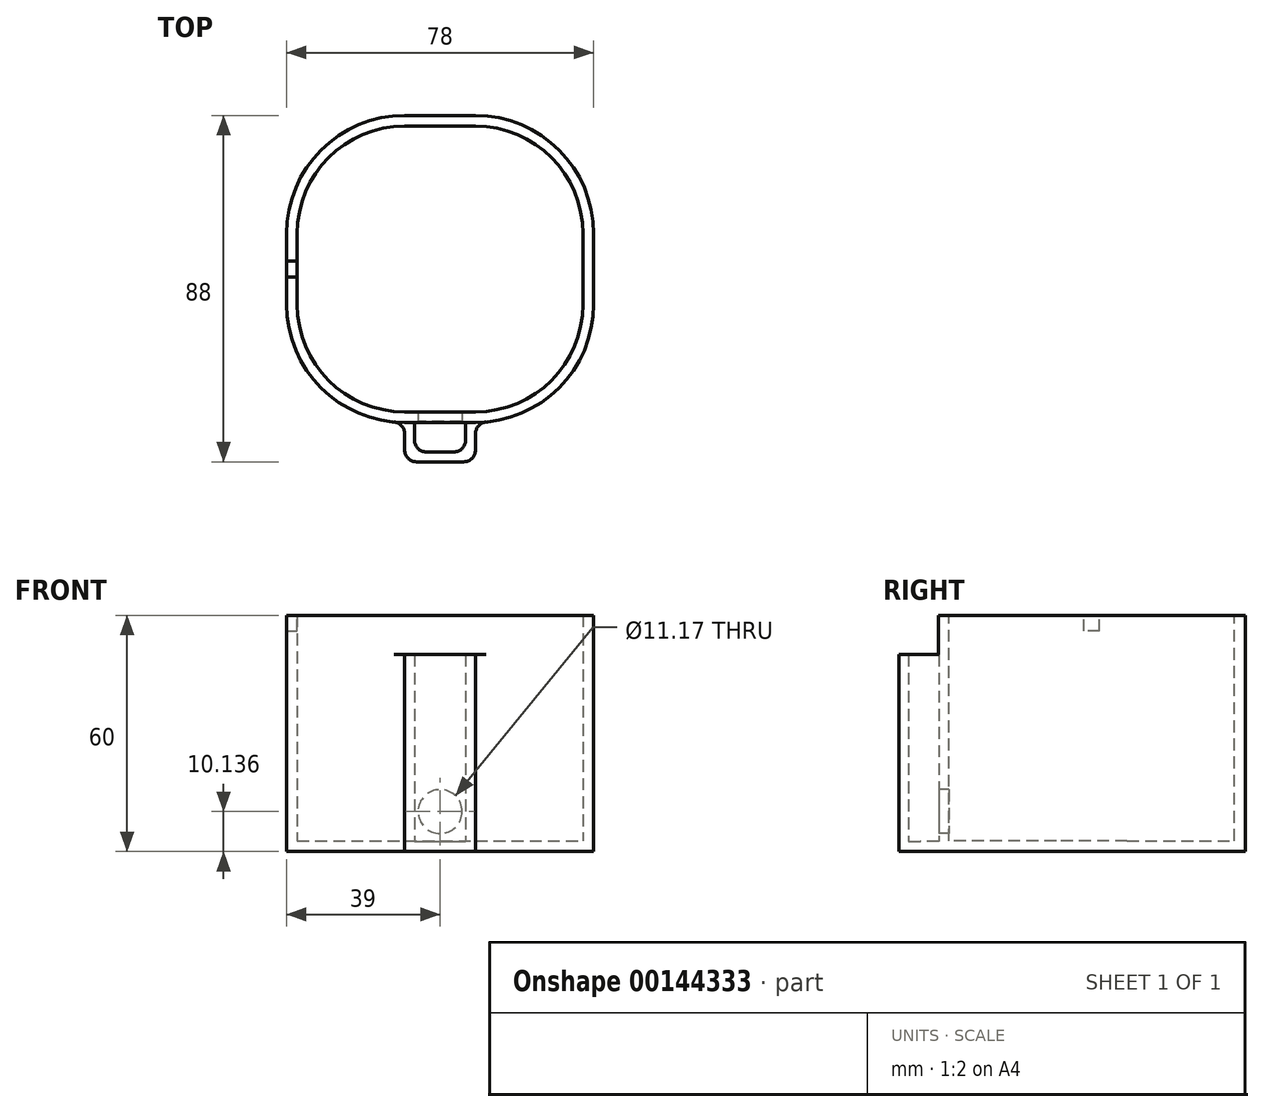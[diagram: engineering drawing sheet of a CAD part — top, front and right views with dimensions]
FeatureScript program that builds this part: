
annotation { "Feature Type Name" : "Feature", "Feature Type Description" : "" }
export const myFeature = defineFeature(function(context is Context, id is Id, definition is map)
    precondition{}
    {
        {
            var Q0;
            Q0=qCreatedBy(makeId("Top.planeOp"),FACE);
            var sketch = newSketch(context, id + "F0", { "sketchPlane" : qUnion([Q0])});
            skLineSegment(sketch, "E0.bottom", {"start": v(-39, 39) * mm, "end": v(39, 39) * mm});
            skLineSegment(sketch, "E0.top", {"start": v(-39, -39) * mm, "end": v(39, -39) * mm});
            skLineSegment(sketch, "E0.left", {"start": v(-39, 39) * mm, "end": v(-39, -39) * mm});
            skLineSegment(sketch, "E0.right", {"start": v(39, 39) * mm, "end": v(39, -39) * mm});
            skSolve(sketch);
        }
        {
            var Q0;
            Q0=makeQuery(id+"F0.imprint","IMPRINT",FACE,{"disambiguationData":[TD([[makeQuery(id+"F0.imprint","IMPRINT",EDGE,{"derivedFrom":sQuery(id+"F0.wireOp",EDGE,"E0.bottom")}),-1.0]])]});
            extrude(context, id + "F1", {"entities" : qUnion([Q0]), "depth" : 60 * mm});
        }
        {
            var Q0;
            Q0=makeQuery(id+"F1.opExtrude","SWEPT_EDGE",EDGE,{"disambiguationData":[OSD([sQuery(id+"F0.wireOp",EDGE,"E0.top"),sQuery(id+"F0.wireOp",EDGE,"E0.left")])]});
            var Q1;
            Q1=makeQuery(id+"F1.opExtrude","SWEPT_EDGE",EDGE,{"disambiguationData":[OSD([sQuery(id+"F0.wireOp",EDGE,"E0.top"),sQuery(id+"F0.wireOp",EDGE,"E0.right")])]});
            var Q2;
            Q2=makeQuery(id+"F1.opExtrude","SWEPT_EDGE",EDGE,{"disambiguationData":[OSD([sQuery(id+"F0.wireOp",EDGE,"E0.bottom"),sQuery(id+"F0.wireOp",EDGE,"E0.right")])]});
            var Q3;
            Q3=makeQuery(id+"F1.opExtrude","SWEPT_EDGE",EDGE,{"disambiguationData":[OSD([sQuery(id+"F0.wireOp",EDGE,"E0.bottom"),sQuery(id+"F0.wireOp",EDGE,"E0.left")])]});
            fillet(context, id + "F2", {"entities" : qUnion([Q0, Q1, Q2, Q3]), "radius" : 30 * mm, "tangentPropagation" : true, "allowEdgeOverflow" : false});
        }
        {
            var Q0;
            Q0=qCreatedBy(makeId("Top.planeOp"),FACE);
            var sketch = newSketch(context, id + "F3", { "sketchPlane" : qUnion([Q0])});
            skPoint(sketch, "E1", {"position": v(-9, -39) * mm});
            skPoint(sketch, "E2", {"position": v(9, -39) * mm});
            skLineSegment(sketch, "E3.bottom", {"start": v(-9, -39) * mm, "end": v(9, -39) * mm});
            skLineSegment(sketch, "E3.top", {"start": v(-9, -49) * mm, "end": v(9, -49) * mm});
            skLineSegment(sketch, "E3.left", {"start": v(-9, -39) * mm, "end": v(-9, -49) * mm});
            skLineSegment(sketch, "E3.right", {"start": v(9, -39) * mm, "end": v(9, -49) * mm});
            skSolve(sketch);
        }
        {
            var Q0;
            Q0=makeQuery(id+"F1.opExtrude","CAP_FACE",FACE,{"disambiguationData":[OSD([sQuery(id+"F0.wireOp",EDGE,"E0.bottom"),sQuery(id+"F0.wireOp",EDGE,"E0.top"),sQuery(id+"F0.wireOp",EDGE,"E0.left"),sQuery(id+"F0.wireOp",EDGE,"E0.right")])],"isStart":false});
            shell(context, id + "F4", {"entities" : qUnion([Q0]), "thickness" : 2.7 * mm});
        }
        {
            var Q0;
            Q0 = qSketchRegion(id + "F3", true);
            extrude(context, id + "F5", {"entities" : qUnion([Q0]), "operationType" : NewBodyOperationType.REMOVE, "oppositeDirection" : true, "depth" : 25 * mm});
        }
        {
            var Q0;
            Q0=makeQuery(id+"F3.imprint","IMPRINT",FACE,{"disambiguationData":[TD([[makeQuery(id+"F3.imprint","IMPRINT",EDGE,{"derivedFrom":sQuery(id+"F3.wireOp",EDGE,"E3.bottom")}),-1.0]])]});
            extrude(context, id + "F6", {"entities" : qUnion([Q0]), "operationType" : NewBodyOperationType.ADD, "depth" : 50 * mm});
        }
        {
            var Q0;
            Q0=makeQuery(id+"F6.opExtrude","CAP_FACE",FACE,{"disambiguationData":[OSD([sQuery(id+"F3.wireOp",EDGE,"E3.bottom"),sQuery(id+"F3.wireOp",EDGE,"E3.top"),sQuery(id+"F3.wireOp",EDGE,"E3.left"),sQuery(id+"F3.wireOp",EDGE,"E3.right")])],"isStart":false});
            shell(context, id + "F7", {"entities" : qUnion([Q0]), "thickness" : 2.5 * mm});
        }
        {
            var Q0;
            Q0=makeQuery(id+"F1.opExtrude","SWEPT_FACE",FACE,{"disambiguationData":[OSD([sQuery(id+"F0.wireOp",EDGE,"E0.top")])]});
            var sketch = newSketch(context, id + "F8", { "sketchPlane" : qUnion([Q0])});
            skCircle(sketch, "E4", {"center": v(0, 10.14) * mm, "radius": 5.59 * mm});
            skSolve(sketch);
        }
        {
            var Q0;
            Q0=makeQuery(id+"F8.imprint","IMPRINT",FACE,{"disambiguationData":[TD([[makeQuery(id+"F8.imprint","IMPRINT",EDGE,{"derivedFrom":sQuery(id+"F8.wireOp",EDGE,"E4")}),1.0]])]});
            extrude(context, id + "F9", {"entities" : qUnion([Q0]), "operationType" : NewBodyOperationType.REMOVE, "oppositeDirection" : true, "depth" : 25 * mm});
        }
        {
            var Q0;
            Q0=makeQuery(id+"F6.opExtrude","SWEPT_EDGE",EDGE,{"disambiguationData":[OSD([sQuery(id+"F3.wireOp",EDGE,"E3.top"),sQuery(id+"F3.wireOp",EDGE,"E3.left")])]});
            var Q1;
            Q1=makeQuery(id+"F6.opExtrude","SWEPT_EDGE",EDGE,{"disambiguationData":[OSD([sQuery(id+"F3.wireOp",EDGE,"E3.top"),sQuery(id+"F3.wireOp",EDGE,"E3.right")])]});
            var Q2;
            Q2=makeQuery(id+"F7.opShell","OFFSET_EDGE",EDGE,{"disambiguationData":[OSD([sQuery(id+"F3.wireOp",EDGE,"E3.top"),sQuery(id+"F3.wireOp",EDGE,"E3.left")])]});
            var Q3;
            Q3=makeQuery(id+"F7.opShell","OFFSET_EDGE",EDGE,{"disambiguationData":[OSD([sQuery(id+"F3.wireOp",EDGE,"E3.top"),sQuery(id+"F3.wireOp",EDGE,"E3.right")])]});
            var Q4;
            {var subQ0=sQuery(id+"F0.wireOp",EDGE,"E0.top");Q4=makeQuery(id+"F6.boolean.opBoolean","MERGE",EDGE,{"derivedFrom":[makeQuery(id+"F2.opFillet","BLEND_EDGE",EDGE,{"blendedFrom":[makeQuery(id+"F1.opExtrude","SWEPT_EDGE",EDGE,{"disambiguationData":[OSD([subQ0,sQuery(id+"F0.wireOp",EDGE,"E0.left")])]}),makeQuery(id+"F1.opExtrude","SWEPT_FACE",FACE,{"disambiguationData":[OSD([subQ0])]})],"blendedInto":[makeQuery(id+"F1.opExtrude","SWEPT_FACE",FACE,{"disambiguationData":[OSD([subQ0])]})]}),makeQuery(id+"F6.opExtrude","SWEPT_EDGE",EDGE,{"disambiguationData":[OSD([sQuery(id+"F3.wireOp",EDGE,"E3.bottom"),sQuery(id+"F3.wireOp",EDGE,"E3.left")])]})]});}
            var Q5;
            {var subQ0=sQuery(id+"F0.wireOp",EDGE,"E0.top");Q5=makeQuery(id+"F6.boolean.opBoolean","MERGE",EDGE,{"derivedFrom":[makeQuery(id+"F2.opFillet","BLEND_EDGE",EDGE,{"blendedFrom":[makeQuery(id+"F1.opExtrude","SWEPT_EDGE",EDGE,{"disambiguationData":[OSD([subQ0,sQuery(id+"F0.wireOp",EDGE,"E0.right")])]}),makeQuery(id+"F1.opExtrude","SWEPT_FACE",FACE,{"disambiguationData":[OSD([subQ0])]})],"blendedInto":[makeQuery(id+"F1.opExtrude","SWEPT_FACE",FACE,{"disambiguationData":[OSD([subQ0])]})]}),makeQuery(id+"F6.opExtrude","SWEPT_EDGE",EDGE,{"disambiguationData":[OSD([sQuery(id+"F3.wireOp",EDGE,"E3.bottom"),sQuery(id+"F3.wireOp",EDGE,"E3.right")])]})]});}
            fillet(context, id + "F10", {"entities" : qUnion([Q0, Q1, Q2, Q3, Q4, Q5]), "radius" : 3 * mm, "tangentPropagation" : true, "allowEdgeOverflow" : false});
        }
        {
            var Q0;
            Q0=makeQuery(id+"F1.opExtrude","CAP_FACE",FACE,{"disambiguationData":[OSD([sQuery(id+"F0.wireOp",EDGE,"E0.bottom"),sQuery(id+"F0.wireOp",EDGE,"E0.top"),sQuery(id+"F0.wireOp",EDGE,"E0.left"),sQuery(id+"F0.wireOp",EDGE,"E0.right")])],"isStart":false});
            var sketch = newSketch(context, id + "F11", { "sketchPlane" : qUnion([Q0])});
            skLineSegment(sketch, "E5", {"start": v(-39, -2) * mm, "end": v(-36.3, -2) * mm});
            skLineSegment(sketch, "E6", {"start": v(-36.3, -2) * mm, "end": v(-36.3, 2) * mm});
            skLineSegment(sketch, "E7", {"start": v(-36.3, 2) * mm, "end": v(-39, 2) * mm});
            skLineSegment(sketch, "E8", {"start": v(-39, 2) * mm, "end": v(-39, -2) * mm});
            skSolve(sketch);
        }
        {
            var Q0;
            Q0 = qSketchRegion(id + "F11", true);
            extrude(context, id + "F12", {"entities" : qUnion([Q0]), "operationType" : NewBodyOperationType.REMOVE, "oppositeDirection" : true, "depth" : 4 * mm});
        }
    });
